# Revit family: Alcorque Taulat
name_source: partatom
category: Furniture
units: mm (PartAtom-declared; Revit-internal decimal feet)

## family parameters
Always vertical = Yes
Cut with Voids When Loaded = No
OmniClass Number = 23.40.20.00
OmniClass Title = General Furniture and Specialties
Room Calculation Point = No
Shared = No
Work Plane-Based = No

## types (4) — shared parameters
Fabricante = BENITO URBAN SL
Ficha_Tecnica = https://www.benito.com
H = 0.04 m
Material = Acero Ferrus
Type Comments = A25A con 3 aberturas circulares. A26A, A27A y A29A con 4 aberturas circulares.
URL_Producto = https://www.benito.com
zero-valued in all types: Default Elevation

## per-type parameters (varying)
| type | A | B | D | Description |
| Alcorque Taulat-A25A-795mm | 0.795 m | 0.795 m | 0.3 m | Alcorque fabricado en acero con tratamiento Ferrus, proceso protector del hierro que garantiza una óptima resistencia a la corrosión. |
| Alcorque Taulat-A26A-995mm | 0.995 m | 0.995 m | 0.3 m | Alcorque fabricado en acero con tratamiento Ferrus, proceso protector del hierro que garantiza una óptima resistencia a la corrosión |
| Alcorque Taulat-A27A-1195mm | 1.195 m | 1.195 m | 0.47 m | Alcorque fabricado en acero con tratamiento Ferrus, proceso protector del hierro que garantiza una óptima resistencia a la corrosión |
| Alcorque Taulat-A29A-1495mm | 1.495 m | 1.495 m | 0.5 m | Alcorque fabricado en acero con tratamiento Ferrus, proceso protector del hierro que garantiza una óptima resistencia a la corrosión |

type visibility flags: 4 boolean params named "<type name>" — each type sets only its own to Yes (folded from table)

## geometry (parser evidence)
native form markers: Blend x2, Sweep x11
no freeform markers — native parametric forms only
